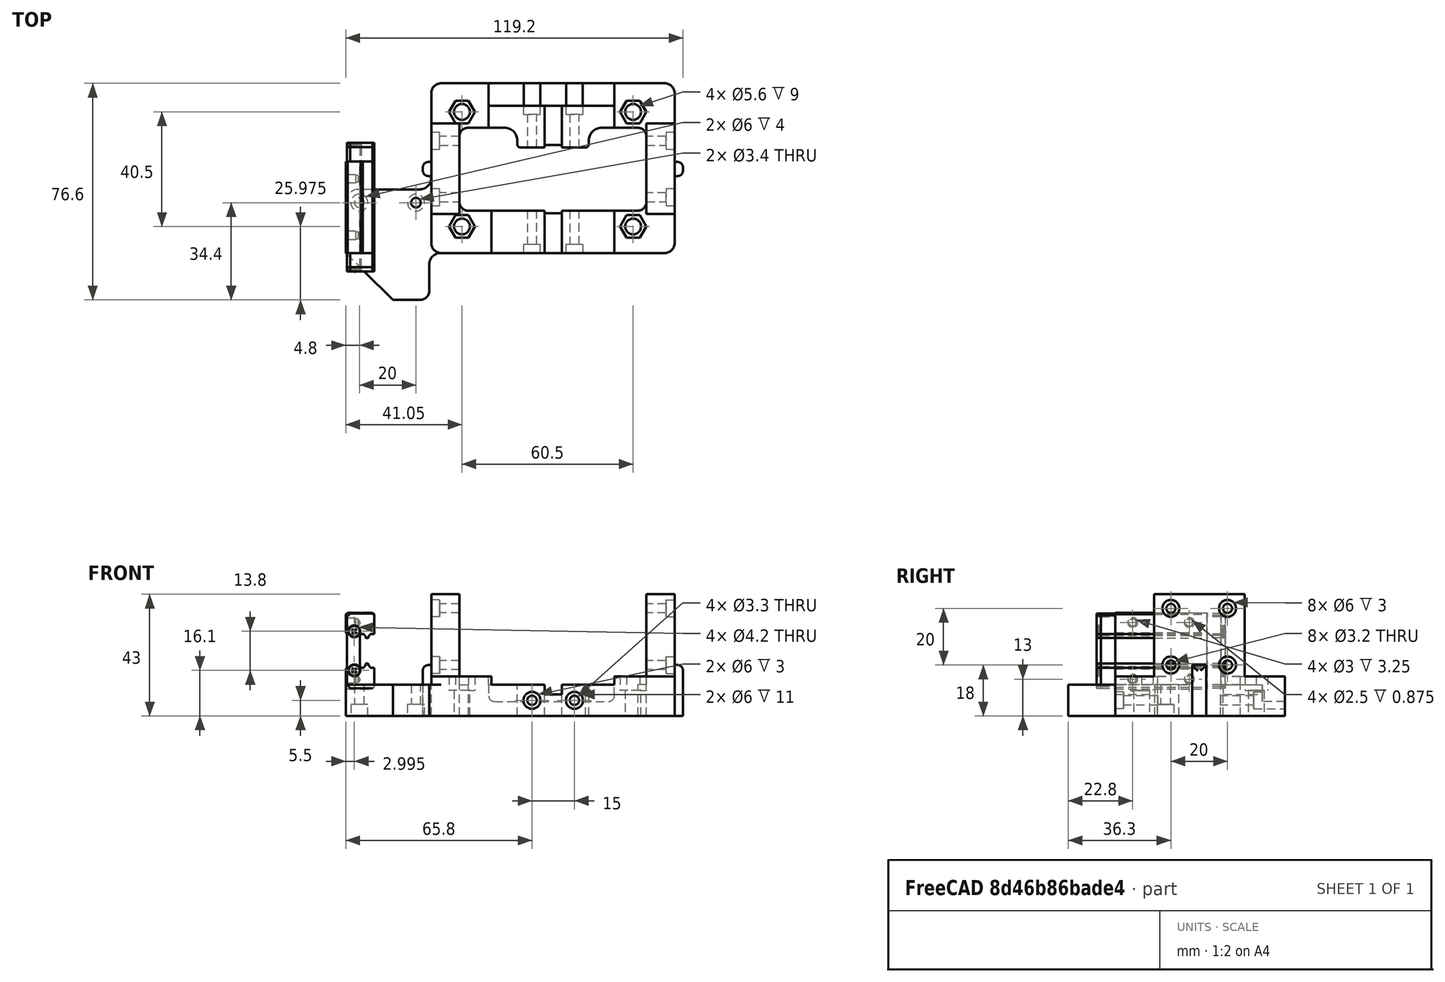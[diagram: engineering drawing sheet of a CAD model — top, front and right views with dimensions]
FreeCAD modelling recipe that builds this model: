
FCSTD DOCUMENT  (FreeCAD 0.19R24291 (Git))
Label: Carriage Mount v2
License: All rights reserved
LicenseURL: http://en.wikipedia.org/wiki/All_rights_reserved
objects: Sketcher::SketchObject×15, PartDesign::Pocket×10, Part::Feature×9, PartDesign::Pad×5, Mesh::Feature×2, PartDesign::Fillet×2, App::Part×1, PartDesign::Body×1, Part::Fillet×1
note: 60 computed .brp shape members not serialized (recipe doc carries the construction recipe); baked Part::Feature solids carry a one-line shape summary decoded from their .brp

FEATURE [Mesh::Feature] y_axis_bed_carriage
  Placement = pos=(-82,-78.3,0) rot=(0,0,1;0rad)
FEATURE [Mesh::Feature] _a__y_belt_clip_x2  label="[a]_y_belt_clip_x2"
  Placement = pos=(-67,-7,115.5) rot=(1,0,0;4.71239rad)
FEATURE [Part::Feature] Part__Feature122  label="MGN12H, LINEAR GUIDE BLOCK v008"
  Placement = pos=(-22.7,16.2,23) rot=(0.57735,-0.57735,0.57735;2.0944rad)
  shape: bbox 4.316 x 1.614 x 4.52 mm, 16 faces (baked)
FEATURE [Part::Feature] Part__Feature121  label="MGN12H, LINEAR GUIDE BLOCK v007"
  Placement = pos=(-22.7,16.2,23) rot=(0.57735,-0.57735,0.57735;2.0944rad)
  shape: bbox 4.36 x 1.614 x 4.223 mm, 16 faces (baked)
FEATURE [Part::Feature] Part__Feature115  label="MGN12H, LINEAR GUIDE BLOCK v1"
  Placement = pos=(-22.7,16.2,23) rot=(0.57735,-0.57735,0.57735;2.0944rad)
  shape: bbox 10 x 32.4 x 27 mm, 66 faces (baked)
FEATURE [Part::Feature] Part__Feature123  label="MGN12H, LINEAR GUIDE BLOCK v009"
  Placement = pos=(-22.7,16.2,23) rot=(0.57735,-0.57735,0.57735;2.0944rad)
  shape: bbox 4.36 x 1.614 x 4.223 mm, 16 faces (baked)
FEATURE [Part::Feature] Part__Feature119  label="MGN12H, LINEAR GUIDE BLOCK v005"
  Placement = pos=(-22.7,16.2,23) rot=(0.57735,-0.57735,0.57735;2.0944rad)
  shape: bbox 9.6 x 1.5 x 26.4 mm, 42 faces (baked)
FEATURE [Part::Feature] Part__Feature120  label="MGN12H, LINEAR GUIDE BLOCK v006"
  Placement = pos=(-22.7,16.2,23) rot=(0.57735,-0.57735,0.57735;2.0944rad)
  shape: bbox 4.316 x 1.614 x 4.52 mm, 16 faces (baked)
FEATURE [Part::Feature] Part__Feature118  label="MGN12H, LINEAR GUIDE BLOCK v004"
  Placement = pos=(-22.7,16.2,23) rot=(0.57735,-0.57735,0.57735;2.0944rad)
  shape: bbox 9.6 x 1.5 x 26.4 mm, 42 faces (baked)
FEATURE [Part::Feature] Part__Feature116  label="MGN12H, LINEAR GUIDE BLOCK v002"
  Placement = pos=(-22.7,16.2,23) rot=(0.57735,-0.57735,0.57735;2.0944rad)
  shape: bbox 9.6 x 5 x 26.4 mm, 40 faces (baked)
FEATURE [Part::Feature] Part__Feature117  label="MGN12H, LINEAR GUIDE BLOCK v003"
  Placement = pos=(-22.7,16.2,23) rot=(0.57735,-0.57735,0.57735;2.0944rad)
  shape: bbox 9.6 x 5 x 26.4 mm, 40 faces (baked)
FEATURE [App::Part] MGN12H__LINEAR_GUIDE_BLOCK_v1  label="MGN12H, LINEAR GUIDE BLOCK v010"
  Group = -> [Part__Feature115,Part__Feature116,Part__Feature117,Part__Feature118,Part__Feature119,Part__Feature120,Part__Feature121,Part__Feature122,Part__Feature123]
  Origin = -> Origin028
  Placement = pos=(40.5,13.5,5) rot=(0,0,1;0rad)
FEATURE [Sketcher::SketchObject] Sketch
  FullyConstrained = true
  MapMode = 5
  Support = -> [XY_Plane]
  sketch-geometry (49):
    g0: LineSegment StartX=3.3 StartY=0 StartZ=0 EndX=82.5 EndY=0 EndZ=0
    g1: LineSegment StartX=86 StartY=3.5 StartZ=0 EndX=86 EndY=56.5 EndZ=0
    g2: LineSegment StartX=82.5 StartY=60 StartZ=0 EndX=3.5 EndY=60 EndZ=0
    g3: LineSegment StartX=0 StartY=56.5 StartZ=0 EndX=0 EndY=26.5 EndZ=0
    g4: ArcOfCircle CenterX=82.5 CenterY=3.5 CenterZ=0 NormalX=0 NormalY=0 NormalZ=1 AngleXU=0 Radius=3.5 StartAngle=4.71239 EndAngle=6.28319
    g5: ArcOfCircle CenterX=82.5 CenterY=56.5 CenterZ=0 NormalX=0 NormalY=0 NormalZ=1 AngleXU=0 Radius=3.5 StartAngle=7e-16 EndAngle=1.5708
    g6: ArcOfCircle CenterX=3.5 CenterY=56.5 CenterZ=0 NormalX=0 NormalY=0 NormalZ=1 AngleXU=0 Radius=3.5 StartAngle=1.5708 EndAngle=3.14159
    g7: ArcOfCircle CenterX=3.3 CenterY=-4 CenterZ=0 NormalX=0 NormalY=0 NormalZ=1 AngleXU=0 Radius=4 StartAngle=1.5708 EndAngle=3.14159
    g8: LineSegment StartX=-4 StartY=22.5 StartZ=0 EndX=-25.6 EndY=22.5 EndZ=0
    g9: LineSegment StartX=-30.2 StartY=17.9 StartZ=0 EndX=-30.2 EndY=0 EndZ=0
    g10: LineSegment StartX=-30.2 StartY=0 StartZ=0 EndX=-13.6 EndY=-16.6 EndZ=0
    g11: LineSegment StartX=-13.6 StartY=-16.6 StartZ=0 EndX=-4 EndY=-16.6 EndZ=0
    g12: LineSegment StartX=-0.7 StartY=-13.3 StartZ=0 EndX=-0.7 EndY=-4 EndZ=0
    g13: ArcOfCircle CenterX=-4 CenterY=-13.3 CenterZ=0 NormalX=0 NormalY=0 NormalZ=1 AngleXU=0 Radius=3.3 StartAngle=4.71239 EndAngle=6.28319
    g14: ArcOfCircle CenterX=-4 CenterY=26.5 CenterZ=0 NormalX=0 NormalY=0 NormalZ=1 AngleXU=0 Radius=4 StartAngle=4.71239 EndAngle=6.28319
    g15: ArcOfCircle CenterX=-25.6 CenterY=17.9 CenterZ=0 NormalX=0 NormalY=0 NormalZ=1 AngleXU=0 Radius=4.6 StartAngle=1.5708 EndAngle=3.14159
    g16: Circle CenterX=-25.4 CenterY=17.8 CenterZ=0 NormalX=0 NormalY=0 NormalZ=1 AngleXU=0 Radius=1.7
    g17: Circle CenterX=-5.4 CenterY=17.8 CenterZ=0 NormalX=0 NormalY=0 NormalZ=1 AngleXU=0 Radius=1.7
    g18: Circle CenterX=10.85 CenterY=9.375 CenterZ=0 NormalX=0 NormalY=0 NormalZ=1 AngleXU=0 Radius=2.8
    g19: Circle CenterX=10.85 CenterY=49.875 CenterZ=0 NormalX=0 NormalY=0 NormalZ=1 AngleXU=0 Radius=2.8
    g20: LineSegment StartX=10.85 StartY=9.375 StartZ=0 EndX=10.85 EndY=49.875 EndZ=0
    g21: Circle CenterX=71.35 CenterY=9.375 CenterZ=0 NormalX=0 NormalY=0 NormalZ=1 AngleXU=0 Radius=2.8
    g22: LineSegment StartX=10.85 StartY=9.375 StartZ=0 EndX=71.35 EndY=9.375 EndZ=0
    g23: Circle CenterX=71.35 CenterY=49.875 CenterZ=0 NormalX=0 NormalY=0 NormalZ=1 AngleXU=0 Radius=2.8
    g24: LineSegment StartX=71.35 StartY=9.375 StartZ=0 EndX=71.35 EndY=49.875 EndZ=0
    g25: LineSegment StartX=13 StartY=44.275 StartZ=0 EndX=25.9042 EndY=44.275 EndZ=0
    g26: LineSegment StartX=76 StartY=41.2768 StartZ=0 EndX=76 EndY=17.975 EndZ=0
    g27: LineSegment StartX=73 StartY=14.975 StartZ=0 EndX=46.2 EndY=14.975 EndZ=0
    g28: LineSegment StartX=10 StartY=17.9683 StartZ=0 EndX=10 EndY=41.275 EndZ=0
    g29: ArcOfCircle CenterX=13 CenterY=17.9683 CenterZ=0 NormalX=0 NormalY=0 NormalZ=1 AngleXU=0 Radius=3 StartAngle=3.14159 EndAngle=4.77911
    g30: ArcOfCircle CenterX=73 CenterY=17.975 CenterZ=0 NormalX=0 NormalY=0 NormalZ=1 AngleXU=0 Radius=3 StartAngle=4.71239 EndAngle=6.28319
    g31: ArcOfCircle CenterX=13 CenterY=41.275 CenterZ=0 NormalX=0 NormalY=0 NormalZ=1 AngleXU=0 Radius=3 StartAngle=1.5708 EndAngle=3.14159
    g32: ArcOfCircle CenterX=73 CenterY=41.2768 CenterZ=0 NormalX=0 NormalY=0 NormalZ=1 AngleXU=0 Radius=3 StartAngle=1e-15 EndAngle=1.53606
    g33: LineSegment StartX=30.4 StartY=39.7792 StartZ=0 EndX=30.4 EndY=38.475 EndZ=0
    g34: LineSegment StartX=31.6 StartY=37.275 StartZ=0 EndX=40 EndY=37.275 EndZ=0
    g35: LineSegment StartX=55.7 StartY=38.4708 StartZ=0 EndX=55.7 EndY=39.775 EndZ=0
    g36: LineSegment StartX=60.2 StartY=44.275 StartZ=0 EndX=73.1042 EndY=44.275 EndZ=0
    g37: ArcOfCircle CenterX=25.9042 CenterY=39.7792 CenterZ=0 NormalX=0 NormalY=0 NormalZ=1 AngleXU=0 Radius=4.49583 StartAngle=1e-16 EndAngle=1.5708
    g38: ArcOfCircle CenterX=60.2 CenterY=39.775 CenterZ=0 NormalX=0 NormalY=0 NormalZ=1 AngleXU=0 Radius=4.5 StartAngle=1.5708 EndAngle=3.14159
    g39: ArcOfCircle CenterX=54.5 CenterY=38.4708 CenterZ=0 NormalX=0 NormalY=0 NormalZ=1 AngleXU=0 Radius=1.2 StartAngle=4.79582 EndAngle=6.28319
    g40: ArcOfCircle CenterX=31.6 CenterY=38.475 CenterZ=0 NormalX=0 NormalY=0 NormalZ=1 AngleXU=0 Radius=1.2 StartAngle=3.14159 EndAngle=4.71239
    g41: LineSegment StartX=40 StartY=37.275 StartZ=0 EndX=40 EndY=38.175 EndZ=0
    g42: LineSegment StartX=40 StartY=38.175 StartZ=0 EndX=46.2 EndY=38.175 EndZ=0
    g43: LineSegment StartX=46.2 StartY=38.175 StartZ=0 EndX=46.2 EndY=37.275 EndZ=0
    g44: LineSegment StartX=46.2 StartY=37.275 StartZ=0 EndX=54.6 EndY=37.275 EndZ=0
    g45: LineSegment StartX=40 StartY=14.975 StartZ=0 EndX=40 EndY=14.075 EndZ=0
    g46: LineSegment StartX=40 StartY=14.075 StartZ=0 EndX=46.2 EndY=14.075 EndZ=0
    g47: LineSegment StartX=46.2 StartY=14.075 StartZ=0 EndX=46.2 EndY=14.975 EndZ=0
    g48: LineSegment StartX=40 StartY=14.975 StartZ=0 EndX=13.2 EndY=14.975 EndZ=0
  constraints (131):
    c: Horizontal(g0)
    c: Horizontal(g2)
    c: Vertical(g1)
    c: Vertical(g3)
    c: Tangent(g0,g4) = -1.5708
    c: Tangent(g1,g4) = -1.5708
    c: Tangent(g1,g5) = -1.5708
    c: Tangent(g2,g5) = -1.5708
    c: Tangent(g3,g6) = -1.5708
    c: Tangent(g2,g6) = -1.5708
    c: PointOnObject(g0,g-1)
    c: DistanceY(g-1,g2) = 60
    c: Radius(g6) = 3.5
    c: Coincident(g7,g0)
    c: Horizontal(g8)
    c: PointOnObject(g9,g-1)
    c: Vertical(g9)
    c: Coincident(g9,g10)
    c: Coincident(g10,g11)
    c: Horizontal(g11)
    c: Coincident(g12,g7)
    c: Vertical(g12)
    c: Tangent(g11,g13) = -1.5708
    c: Tangent(g12,g13) = -1.5708
    c: Tangent(g8,g14) = 1.5708
    c: Tangent(g3,g14) = 1.5708
    c: Tangent(g9,g15) = -1.5708
    c: Tangent(g8,g15) = -1.5708
    c: PointOnObject(g3,g-2)
    c: Equal(g6,g5)
    c: Equal(g5,g4)
    c: Angle(g7) = 1.5708
    c: DistanceY(g-1,g8) = 22.5
    c: DistanceX(g9,g-1) = 30.2
    c: DistanceY(g11,g-1) = 16.6
    c: DistanceX(g7,g-1) = 0.7
    c: Distance(g12) = 9.3
    c: Radius(g7) = 4
    c: DistanceX(g11,g11) = 9.6
    c: Radius(g15) = 4.6
    c: Radius(g14) = 4
    c: DistanceX(g3,g1) = 86
    c: DistanceY(g7,g-1) = 4
    c: Radius(g16) = 1.7
    c: Equal(g16,g17) = 1.7
    c: Horizontal(g16,g17)
    c: DistanceX(g17,g-1) = 5.4
    c: DistanceX(g16,g17) = 20
    c: DistanceY(g-1,g17) = 17.8
    c: Radius(g18) = 2.8
    c: DistanceX(g-1,g18) = 10.85
    c: DistanceY(g-1,g18) = 9.375
    c: Radius(g19) = 2.8
    c: Coincident(g18,g20)
    c: Coincident(g19,g20)
    c: Distance(g20) = 40.5
    c: Angle(g20) = 1.5708
    c: Radius(g21) = 2.8
    c: Coincident(g18,g22)
    c: Coincident(g21,g22)
    c: Distance(g22) = 60.5
    c: Perpendicular(g22,g20)
    c: Radius(g23) = 2.8
    c: Coincident(g21,g24)
    c: Coincident(g23,g24)
    c: Equal(g20,g24)
    c: Parallel(g24,g20)
    c: Horizontal(g25)
    c: Horizontal(g27)
    c: Vertical(g26)
    c: Vertical(g28)
    c: Tangent(g28,g29) = 1.5708
    c: Coincident(g48,g29) = 1.5708
    c: Tangent(g27,g30) = 1.5708
    c: Tangent(g26,g30) = 1.5708
    c: Tangent(g28,g31) = 1.5708
    c: Tangent(g25,g31) = 1.5708
    c: Coincident(g36,g32) = 1.5708
    c: Tangent(g26,g32) = 1.5708
    c: Equal(g29,g31)
    c: Equal(g31,g32)
    c: Equal(g32,g30)
    c: Radius(g29) = 3
    c: DistanceX(g-1,g28) = 10
    c: DistanceX(g26,g1) = 10
    c: DistanceY(g18,g48) = 5.6
    c: DistanceY(g25,g19) = 5.6
    c: Vertical(g33)
    c: Horizontal(g34)
    c: Vertical(g35)
    c: Tangent(g25,g36)
    c: Tangent(g25,g37) = 1.5708
    c: Tangent(g33,g37) = 1.5708
    c: Tangent(g35,g38) = 1.5708
    c: Tangent(g36,g38) = 1.5708
    c: Coincident(g44,g39) = -1.5708
    c: Tangent(g35,g39) = -1.5708
    c: Tangent(g33,g40) = -1.5708
    c: Tangent(g34,g40) = -1.5708
    c: Equal(g40,g39)
    c: DistanceY(g34,g25) = 7
    c: DistanceX(g28,g33) = 20.4
    c: DistanceX(g33,g35) = 25.3
    c: Radius(g40) = 1.2
    c: Equal(g33,g35)
    c: Equal(g25,g36)
    c: Radius(g38) = 4.5
    c: Vertical(g41)
    c: Coincident(g41,g42)
    c: Horizontal(g42)
    c: Coincident(g42,g43)
    c: Vertical(g43)
    c: Coincident(g34,g41)
    c: Coincident(g44,g43)
    c: Tangent(g34,g44)
    c: Equal(g34,g44)
    c: DistanceX(g42,g42) = 6.2
    c: DistanceX(g34,g34) = 8.4
    c: DistanceY(g43,g43) = 0.9
    c: Coincident(g45,g46)
    c: Horizontal(g46)
    c: Coincident(g46,g47)
    c: Vertical(g47)
    c: Vertical(g45)
    c: Equal(g42,g46)
    c: Equal(g43,g47)
    c: Coincident(g27,g47)
    c: Coincident(g48,g45)
    c: Tangent(g27,g48)
    c: Equal(g48,g27)
    c: DistanceX(g48,g48) = 26.8
FEATURE [PartDesign::Pad] Pad
  Direction = (1,1,1)
  Length = 11
  Length2 = 100
  Profile = -> Sketch
  Type = 0
FEATURE [Sketcher::SketchObject] Sketch001
  ExternalGeometry = -> [Pad]
  FullyConstrained = true
  MapMode = 5
  Placement = pos=(0,0,11) rot=(0,0,1;0rad)
  Support = -> [Pad]
  sketch-geometry (24):
    g0: LineSegment StartX=3.5 StartY=0 StartZ=0 EndX=21.3 EndY=0 EndZ=0
    g1: LineSegment StartX=21.3 StartY=0 StartZ=0 EndX=21.3 EndY=14.975 EndZ=0
    g2: LineSegment StartX=21.3 StartY=14.975 StartZ=0 EndX=12.9933 EndY=14.975 EndZ=0
    g3: LineSegment StartX=10 StartY=17.9683 StartZ=0 EndX=10 EndY=41.275 EndZ=0
    g4: LineSegment StartX=20.3 StartY=44.275 StartZ=0 EndX=20.3 EndY=60 EndZ=0
    g5: LineSegment StartX=20.3 StartY=60 StartZ=0 EndX=3.5 EndY=60 EndZ=0
    g6: LineSegment StartX=0 StartY=56.5 StartZ=0 EndX=0 EndY=3.5 EndZ=0
    g7: ArcOfCircle CenterX=12.9933 CenterY=17.9683 CenterZ=0 NormalX=0 NormalY=0 NormalZ=1 AngleXU=0 Radius=2.99333 StartAngle=3.14159 EndAngle=4.71239
    g8: ArcOfCircle CenterX=13 CenterY=41.275 CenterZ=0 NormalX=0 NormalY=0 NormalZ=1 AngleXU=0 Radius=3 StartAngle=1.5708 EndAngle=3.14159
    g9: ArcOfCircle CenterX=3.5 CenterY=56.5 CenterZ=0 NormalX=0 NormalY=0 NormalZ=1 AngleXU=0 Radius=3.5 StartAngle=1.5708 EndAngle=3.14159
    g10: LineSegment StartX=13 StartY=44.275 StartZ=0 EndX=20.3 EndY=44.275 EndZ=0
    g11: ArcOfCircle CenterX=3.5 CenterY=3.5 CenterZ=0 NormalX=0 NormalY=0 NormalZ=1 AngleXU=0 Radius=3.5 StartAngle=3.14159 EndAngle=4.71239
    g12: LineSegment StartX=64.7 StartY=0 StartZ=0 EndX=64.7 EndY=14.975 EndZ=0
    g13: LineSegment StartX=64.7 StartY=14.975 StartZ=0 EndX=73 EndY=14.975 EndZ=0
    g14: LineSegment StartX=76 StartY=17.975 StartZ=0 EndX=76 EndY=41.2768 EndZ=0
    g15: LineSegment StartX=73.0018 StartY=44.275 StartZ=0 EndX=64.7018 EndY=44.275 EndZ=0
    g16: LineSegment StartX=64.7018 StartY=44.275 StartZ=0 EndX=64.7018 EndY=60 EndZ=0
    g17: LineSegment StartX=64.7018 StartY=60 StartZ=0 EndX=82.5 EndY=60 EndZ=0
    g18: LineSegment StartX=86 StartY=56.5 StartZ=0 EndX=86 EndY=3.5 EndZ=0
    g19: LineSegment StartX=82.5 StartY=0 StartZ=0 EndX=64.7 EndY=0 EndZ=0
    g20: ArcOfCircle CenterX=73 CenterY=17.975 CenterZ=0 NormalX=0 NormalY=0 NormalZ=1 AngleXU=0 Radius=3 StartAngle=4.71239 EndAngle=6.28319
    g21: ArcOfCircle CenterX=73.0018 CenterY=41.2768 CenterZ=0 NormalX=0 NormalY=0 NormalZ=1 AngleXU=0 Radius=2.99819 StartAngle=1.1e-15 EndAngle=1.5708
    g22: ArcOfCircle CenterX=82.5 CenterY=56.5 CenterZ=0 NormalX=0 NormalY=0 NormalZ=1 AngleXU=0 Radius=3.5 StartAngle=0 EndAngle=1.5708
    g23: ArcOfCircle CenterX=82.5 CenterY=3.5 CenterZ=0 NormalX=0 NormalY=0 NormalZ=1 AngleXU=0 Radius=3.5 StartAngle=4.71239 EndAngle=6.28319
  constraints (56):
    c: PointOnObject(g0,g-1)
    c: Coincident(g0,g1)
    c: PointOnObject(g1,g-3)
    c: Vertical(g1)
    c: Coincident(g1,g2)
    c: Horizontal(g2)
    c: PointOnObject(g4,g-6)
    c: Vertical(g4)
    c: Coincident(g4,g5)
    c: Tangent(g3,g7) = 1.5708
    c: Tangent(g2,g7) = 1.5708
    c: Coincident(g3,g-4)
    c: DistanceX(g-1,g0) = 21.3
    c: Tangent(g3,g8) = 1.5708
    c: Coincident(g-5,g8) = 1.5708
    c: Tangent(g6,g9) = -1.5708
    c: Tangent(g5,g9) = -1.5708
    c: Coincident(g10,g8)
    c: Coincident(g10,g4)
    c: Horizontal(g10)
    c: DistanceX(g6,g4) = 20.3
    c: Coincident(g5,g-6)
    c: PointOnObject(g6,g-2)
    c: Coincident(g3,g-4)
    c: Tangent(g6,g11) = -1.5708
    c: Tangent(g0,g11) = -1.5708
    c: Radius(g11) = 3.5
    c: PointOnObject(g6,g-2)
    c: PointOnObject(g0,g-1)
    c: PointOnObject(g12,g-1)
    c: Vertical(g12)
    c: Coincident(g12,g13)
    c: Horizontal(g15)
    c: Coincident(g15,g16)
    c: PointOnObject(g16,g-6)
    c: Vertical(g16)
    c: Coincident(g16,g17)
    c: Vertical(g18)
    c: Coincident(g19,g12)
    c: Tangent(g13,g20) = -1.5708
    c: Tangent(g14,g20) = -1.5708
    c: Tangent(g15,g21) = -1.5708
    c: Tangent(g14,g21) = -1.5708
    c: Tangent(g17,g22) = 1.5708
    c: Tangent(g18,g22) = 1.5708
    c: Tangent(g19,g23) = 1.5708
    c: Tangent(g18,g23) = 1.5708
    c: Coincident(g18,g-10)
    c: DistanceX(g12,g18) = 21.3
    c: Horizontal(g19)
    c: Coincident(g13,g-8)
    c: Coincident(g14,g-9)
    c: Coincident(g14,g-9)
    c: PointOnObject(g15,g-7)
    c: Equal(g13,g15)
    c: Coincident(g17,g-6)
FEATURE [PartDesign::Pad] Pad001
  BaseFeature = -> Pad
  Direction = (1,1,1)
  Length = 3
  Length2 = 100
  Profile = -> Sketch001
  Type = 0
FEATURE [Sketcher::SketchObject] Sketch002
  ExternalGeometry = -> [Pad]
  FullyConstrained = true
  MapMode = 5
  Placement = pos=(0,0,14) rot=(0,0,1;0rad)
  Support = -> [Pad001]
  sketch-geometry (28):
    g0: LineSegment StartX=13.1594 StartY=5.375 StartZ=0 EndX=15.4688 EndY=9.375 EndZ=0
    g1: LineSegment StartX=15.4688 StartY=9.375 StartZ=0 EndX=13.1594 EndY=13.375 EndZ=0
    g2: LineSegment StartX=13.1594 StartY=13.375 StartZ=0 EndX=8.5406 EndY=13.375 EndZ=0
    g3: LineSegment StartX=8.5406 StartY=13.375 StartZ=0 EndX=6.2312 EndY=9.375 EndZ=0
    g4: LineSegment StartX=6.2312 StartY=9.375 StartZ=0 EndX=8.5406 EndY=5.375 EndZ=0
    g5: LineSegment StartX=8.5406 StartY=5.375 StartZ=0 EndX=13.1594 EndY=5.375 EndZ=0
    g6: Circle CenterX=10.85 CenterY=9.375 CenterZ=0 NormalX=0 NormalY=0 NormalZ=1 AngleXU=0 Radius=4.6188
    g7: LineSegment StartX=13.1594 StartY=45.875 StartZ=0 EndX=15.4688 EndY=49.875 EndZ=0
    g8: LineSegment StartX=15.4688 StartY=49.875 StartZ=0 EndX=13.1594 EndY=53.875 EndZ=0
    g9: LineSegment StartX=13.1594 StartY=53.875 StartZ=0 EndX=8.5406 EndY=53.875 EndZ=0
    g10: LineSegment StartX=8.5406 StartY=53.875 StartZ=0 EndX=6.2312 EndY=49.875 EndZ=0
    g11: LineSegment StartX=6.2312 StartY=49.875 StartZ=0 EndX=8.5406 EndY=45.875 EndZ=0
    g12: LineSegment StartX=8.5406 StartY=45.875 StartZ=0 EndX=13.1594 EndY=45.875 EndZ=0
    g13: Circle CenterX=10.85 CenterY=49.875 CenterZ=0 NormalX=0 NormalY=0 NormalZ=1 AngleXU=0 Radius=4.6188
    g14: LineSegment StartX=73.6594 StartY=45.875 StartZ=0 EndX=75.9688 EndY=49.875 EndZ=0
    g15: LineSegment StartX=75.9688 StartY=49.875 StartZ=0 EndX=73.6594 EndY=53.875 EndZ=0
    g16: LineSegment StartX=73.6594 StartY=53.875 StartZ=0 EndX=69.0406 EndY=53.875 EndZ=0
    g17: LineSegment StartX=69.0406 StartY=53.875 StartZ=0 EndX=66.7312 EndY=49.875 EndZ=0
    g18: LineSegment StartX=66.7312 StartY=49.875 StartZ=0 EndX=69.0406 EndY=45.875 EndZ=0
    g19: LineSegment StartX=69.0406 StartY=45.875 StartZ=0 EndX=73.6594 EndY=45.875 EndZ=0
    g20: Circle CenterX=71.35 CenterY=49.875 CenterZ=0 NormalX=0 NormalY=0 NormalZ=1 AngleXU=0 Radius=4.6188
    g21: LineSegment StartX=73.6594 StartY=5.375 StartZ=0 EndX=75.9688 EndY=9.375 EndZ=0
    g22: LineSegment StartX=75.9688 StartY=9.375 StartZ=0 EndX=73.6594 EndY=13.375 EndZ=0
    g23: LineSegment StartX=73.6594 StartY=13.375 StartZ=0 EndX=69.0406 EndY=13.375 EndZ=0
    g24: LineSegment StartX=69.0406 StartY=13.375 StartZ=0 EndX=66.7312 EndY=9.375 EndZ=0
    g25: LineSegment StartX=66.7312 StartY=9.375 StartZ=0 EndX=69.0406 EndY=5.375 EndZ=0
    g26: LineSegment StartX=69.0406 StartY=5.375 StartZ=0 EndX=73.6594 EndY=5.375 EndZ=0
    g27: Circle CenterX=71.35 CenterY=9.375 CenterZ=0 NormalX=0 NormalY=0 NormalZ=1 AngleXU=0 Radius=4.6188
  constraints (64):
    c: Coincident(g0,g1)
    c: Coincident(g1,g2)
    c: Coincident(g2,g3)
    c: Coincident(g3,g4)
    c: Coincident(g4,g5)
    c: Coincident(g5,g0)
    c: Equal(g0, g1-g5) x5
    c: PointOnObject(g0,g6)
    c: PointOnObject(g1,g6)
    c: PointOnObject(g2,g6)
    c: PointOnObject(g3,g6)
    c: PointOnObject(g4,g6)
    c: PointOnObject(g5,g6)
    c: Coincident(g6,g-3)
    c: Horizontal(g2)
    c: DistanceY(g4,g2) = 8
    c: Coincident(g7,g8)
    c: Coincident(g8,g9)
    c: Coincident(g9,g10)
    c: Coincident(g10,g11)
    c: Coincident(g11,g12)
    c: Coincident(g12,g7)
    c: Equal(g7, g8-g12) x5
    c: PointOnObject(g7,g13)
    c: PointOnObject(g8,g13)
    c: PointOnObject(g9,g13)
    c: PointOnObject(g10,g13)
    c: PointOnObject(g11,g13)
    c: PointOnObject(g12,g13)
    c: Coincident(g13,g-4)
    c: Coincident(g14,g15)
    c: Coincident(g15,g16)
    c: Coincident(g16,g17)
    c: Coincident(g17,g18)
    c: Coincident(g18,g19)
    c: Coincident(g19,g14)
    c: Equal(g14, g15-g19) x5
    c: PointOnObject(g14,g20)
    c: PointOnObject(g15,g20)
    c: PointOnObject(g16,g20)
    c: PointOnObject(g17,g20)
    c: PointOnObject(g18,g20)
    c: PointOnObject(g19,g20)
    c: Coincident(g20,g-5)
    c: Coincident(g21,g22)
    c: Coincident(g22,g23)
    c: Coincident(g23,g24)
    c: Coincident(g24,g25)
    c: Coincident(g25,g26)
    c: Coincident(g26,g21)
    c: Equal(g21, g22-g26) x5
    c: PointOnObject(g21,g27)
    c: PointOnObject(g22,g27)
    c: PointOnObject(g23,g27)
    c: PointOnObject(g24,g27)
    c: PointOnObject(g25,g27)
    c: PointOnObject(g26,g27)
    c: Coincident(g27,g-6)
    c: Horizontal(g23)
    c: DistanceY(g25,g23) = 8
    c: Horizontal(g9)
    c: Horizontal(g16)
    c: DistanceY(g11,g9) = 8
    c: DistanceY(g18,g16) = 8
FEATURE [PartDesign::Pocket] Pocket
  BaseFeature = -> Pad001
  Length = 5
  Length2 = 100
  Profile = -> Sketch002
  Type = 0
FEATURE [Sketcher::SketchObject] Sketch003
  ExternalGeometry = -> [Pocket]
  FullyConstrained = true
  MapMode = 5
  Placement = pos=(0,0,0) rot=(1,0,0;1.5708rad)
  Support = -> [Pocket]
  sketch-geometry (2):
    g0: Circle CenterX=35.6 CenterY=5.5 CenterZ=0 NormalX=0 NormalY=0 NormalZ=1 AngleXU=0 Radius=1.65
    g1: Circle CenterX=50.6 CenterY=5.5 CenterZ=0 NormalX=0 NormalY=0 NormalZ=1 AngleXU=0 Radius=1.65
  constraints (6):
    c: Radius(g0) = 1.65
    c: Equal(g0,g1)
    c: DistanceX(g0,g1) = 15
    c: DistanceX(g-1,g0) = 35.6
    c: DistanceY(g-1,g0) = 5.5
    c: Horizontal(g0,g1)
FEATURE [PartDesign::Pocket] Pocket001
  BaseFeature = -> Pocket
  Length = 60
  Length2 = 100
  Profile = -> Sketch003
  Type = 0
FEATURE [Sketcher::SketchObject] Sketch004
  ExternalGeometry = -> [Pocket001]
  FullyConstrained = true
  MapMode = 5
  Placement = pos=(0,0,0) rot=(1,0,0;1.5708rad)
  Support = -> [Pocket001]
  sketch-geometry (2):
    g0: Circle CenterX=35.6 CenterY=5.5 CenterZ=0 NormalX=0 NormalY=0 NormalZ=1 AngleXU=0 Radius=3
    g1: Circle CenterX=50.6 CenterY=5.5 CenterZ=0 NormalX=0 NormalY=0 NormalZ=1 AngleXU=0 Radius=3
  constraints (4):
    c: Radius(g0) = 3
    c: Equal(g0,g1)
    c: Coincident(g1,g-4)
    c: Coincident(g0,g-3)
FEATURE [PartDesign::Pocket] Pocket002
  BaseFeature = -> Pocket001
  Length = 3
  Length2 = 100
  Profile = -> Sketch004
  Type = 0
FEATURE [Sketcher::SketchObject] Sketch005
  ExternalGeometry = -> [Pocket002]
  FullyConstrained = true
  MapMode = 5
  Placement = pos=(0,0,0) rot=(1,0,0;3.14159rad)
  Support = -> [Pocket002]
  sketch-geometry (2):
    g0: Circle CenterX=-25.4 CenterY=-17.8 CenterZ=0 NormalX=0 NormalY=0 NormalZ=1 AngleXU=0 Radius=3
    g1: Circle CenterX=-5.4 CenterY=-17.8 CenterZ=0 NormalX=0 NormalY=0 NormalZ=1 AngleXU=0 Radius=3
  constraints (4):
    c: Coincident(g0,g-3)
    c: Coincident(g1,g-4)
    c: Equal(g0,g1)
    c: Radius(g0) = 3
FEATURE [PartDesign::Pocket] Pocket003  label="Belt Cutout"
  BaseFeature = -> Pocket002
  Length = 4
  Length2 = 100
  Profile = -> Sketch005
  Type = 0
FEATURE [Sketcher::SketchObject] Sketch006
  ExternalGeometry = -> [Pocket003]
  FullyConstrained = true
  MapMode = 5
  Placement = pos=(0,0,14) rot=(0,0,1;0rad)
  Support = -> [Pocket003]
  sketch-geometry (8):
    g0: LineSegment StartX=0 StartY=13.8 StartZ=0 EndX=10 EndY=13.8 EndZ=0
    g1: LineSegment StartX=10 StartY=13.8 StartZ=0 EndX=10 EndY=45.8 EndZ=0
    g2: LineSegment StartX=10 StartY=45.8 StartZ=0 EndX=0 EndY=45.8 EndZ=0
    g3: LineSegment StartX=0 StartY=45.8 StartZ=0 EndX=0 EndY=13.8 EndZ=0
    g4: LineSegment StartX=86 StartY=13.8 StartZ=0 EndX=76 EndY=13.8 EndZ=0
    g5: LineSegment StartX=76 StartY=13.8 StartZ=0 EndX=76 EndY=45.8 EndZ=0
    g6: LineSegment StartX=76 StartY=45.8 StartZ=0 EndX=86 EndY=45.8 EndZ=0
    g7: LineSegment StartX=86 StartY=45.8 StartZ=0 EndX=86 EndY=13.8 EndZ=0
  constraints (24):
    c: Coincident(g0,g1)
    c: Coincident(g1,g2)
    c: Coincident(g2,g3)
    c: Coincident(g3,g0)
    c: Horizontal(g0)
    c: Horizontal(g2)
    c: Vertical(g1)
    c: Vertical(g3)
    c: PointOnObject(g0,g-2)
    c: DistanceX(g2,g2) = 10
    c: DistanceY(g3,g3) = 32
    c: DistanceY(g-1,g0) = 13.8
    c: Coincident(g4,g5)
    c: Coincident(g5,g6)
    c: Coincident(g6,g7)
    c: Coincident(g7,g4)
    c: Horizontal(g4)
    c: Horizontal(g6)
    c: Vertical(g5)
    c: Vertical(g7)
    c: PointOnObject(g4,g-3)
    c: PointOnObject(g-4,g5)
    c: Equal(g3,g7)
    c: DistanceY(g-1,g4) = 13.8
FEATURE [PartDesign::Pad] Pad002  label="MGN12H Supports"
  BaseFeature = -> Pocket003
  Direction = (1,1,1)
  Length = 29
  Length2 = 100
  Profile = -> Sketch006
  Type = 0
FEATURE [Sketcher::SketchObject] Sketch007
  FullyConstrained = true
  MapMode = 5
  Placement = pos=(0,0,0) rot=(0.57735,-0.57735,-0.57735;2.0944rad)
  Support = -> [Pad002]
  sketch-geometry (7):
    g0: Circle CenterX=-39.7 CenterY=18 CenterZ=0 NormalX=0 NormalY=0 NormalZ=1 AngleXU=0 Radius=1.6
    g1: Circle CenterX=-39.7 CenterY=38 CenterZ=0 NormalX=0 NormalY=0 NormalZ=1 AngleXU=0 Radius=1.6
    g2: LineSegment StartX=-39.7 StartY=18 StartZ=0 EndX=-39.7 EndY=38 EndZ=0
    g3: Circle CenterX=-19.7 CenterY=18 CenterZ=0 NormalX=0 NormalY=0 NormalZ=1 AngleXU=0 Radius=1.6
    g4: LineSegment StartX=-39.7 StartY=18 StartZ=0 EndX=-19.7 EndY=18 EndZ=0
    g5: Circle CenterX=-19.7 CenterY=38 CenterZ=0 NormalX=0 NormalY=0 NormalZ=1 AngleXU=0 Radius=1.6
    g6: LineSegment StartX=-19.7 StartY=18 StartZ=0 EndX=-19.7 EndY=38 EndZ=0
  constraints (18):
    c: Radius(g0) = 1.6
    c: DistanceY(g-1,g0) = 18
    c: DistanceX(g0,g-1) = 39.7
    c: Radius(g1) = 1.6
    c: Coincident(g0,g2)
    c: Coincident(g1,g2)
    c: Distance(g2) = 20
    c: Angle(g2) = 1.5708
    c: Radius(g3) = 1.6
    c: Coincident(g0,g4)
    c: Coincident(g3,g4)
    c: Distance(g4) = 20
    c: Perpendicular(g4,g2)
    c: Radius(g5) = 1.6
    c: Coincident(g3,g6)
    c: Coincident(g5,g6)
    c: Equal(g2,g6)
    c: Parallel(g6,g2)
FEATURE [PartDesign::Pocket] Pocket004
  BaseFeature = -> Pad002
  Length = 90
  Length2 = 100
  Profile = -> Sketch007
  Type = 0
FEATURE [Sketcher::SketchObject] Sketch008
  ExternalGeometry = -> [Pocket004]
  FullyConstrained = true
  MapMode = 5
  Placement = pos=(0,0,0) rot=(0.57735,-0.57735,-0.57735;2.0944rad)
  Support = -> [Pocket004]
  sketch-geometry (4):
    g0: Circle CenterX=-39.7 CenterY=38 CenterZ=0 NormalX=0 NormalY=0 NormalZ=1 AngleXU=0 Radius=3
    g1: Circle CenterX=-39.7 CenterY=18 CenterZ=0 NormalX=0 NormalY=0 NormalZ=1 AngleXU=0 Radius=3
    g2: Circle CenterX=-19.7 CenterY=38 CenterZ=0 NormalX=0 NormalY=0 NormalZ=1 AngleXU=0 Radius=3
    g3: Circle CenterX=-19.7 CenterY=18 CenterZ=0 NormalX=0 NormalY=0 NormalZ=1 AngleXU=0 Radius=3
  constraints (8):
    c: Coincident(g0,g-3)
    c: Radius(g0) = 3
    c: Equal(g0,g1) = 3
    c: Coincident(g1,g-6)
    c: Equal(g0,g2) = 3
    c: Coincident(g2,g-4)
    c: Equal(g0,g3) = 3
    c: Coincident(g3,g-5)
FEATURE [PartDesign::Pocket] Pocket005
  BaseFeature = -> Pocket004
  Length = 3
  Length2 = 100
  Profile = -> Sketch008
  Type = 0
FEATURE [Sketcher::SketchObject] Sketch009
  ExternalGeometry = -> [Pocket005]
  FullyConstrained = true
  MapMode = 5
  Placement = pos=(86,0,0) rot=(0.57735,0.57735,0.57735;2.0944rad)
  Support = -> [Pocket005]
  sketch-geometry (4):
    g0: Circle CenterX=19.7 CenterY=38 CenterZ=0 NormalX=0 NormalY=0 NormalZ=1 AngleXU=0 Radius=3
    g1: Circle CenterX=19.7 CenterY=18 CenterZ=0 NormalX=0 NormalY=0 NormalZ=1 AngleXU=0 Radius=3
    g2: Circle CenterX=39.7 CenterY=38 CenterZ=0 NormalX=0 NormalY=0 NormalZ=1 AngleXU=0 Radius=3
    g3: Circle CenterX=39.7 CenterY=18 CenterZ=0 NormalX=0 NormalY=0 NormalZ=1 AngleXU=0 Radius=3
  constraints (8):
    c: Radius(g0) = 3
    c: Equal(g0,g1) = 3
    c: Equal(g0,g2) = 3
    c: Equal(g0,g3) = 3
    c: Coincident(g1,g-6)
    c: Coincident(g3,g-5)
    c: Coincident(g2,g-4)
    c: Coincident(g0,g-3)
FEATURE [PartDesign::Pocket] Pocket006
  BaseFeature = -> Pocket005
  Length = 3
  Length2 = 100
  Profile = -> Sketch009
  Type = 0
FEATURE [Sketcher::SketchObject] Sketch010
  ExternalGeometry = -> [Pocket006]
  FullyConstrained = true
  MapMode = 5
  Placement = pos=(0,0,0) rot=(1,0,0;1.5708rad)
  Support = -> [Pocket006]
  sketch-geometry (4):
    g0: LineSegment StartX=40.05 StartY=11 StartZ=0 EndX=46.15 EndY=11 EndZ=0
    g1: LineSegment StartX=46.15 StartY=11 StartZ=0 EndX=46.15 EndY=7.6 EndZ=0
    g2: LineSegment StartX=46.15 StartY=7.6 StartZ=0 EndX=40.05 EndY=7.6 EndZ=0
    g3: LineSegment StartX=40.05 StartY=7.6 StartZ=0 EndX=40.05 EndY=11 EndZ=0
  constraints (12):
    c: Coincident(g0,g1)
    c: Coincident(g1,g2)
    c: Coincident(g2,g3)
    c: Coincident(g3,g0)
    c: Horizontal(g0)
    c: Horizontal(g2)
    c: Vertical(g1)
    c: Vertical(g3)
    c: PointOnObject(g0,g-4)
    c: DistanceX(g0,g0) = 6.1
    c: DistanceX(g-3,g0) = 4.45
    c: DistanceY(g3,g3) = 3.4
FEATURE [PartDesign::Pocket] Pocket007
  BaseFeature = -> Pocket006
  Length = 60
  Length2 = 100
  Profile = -> Sketch010
  Type = 0
FEATURE [Sketcher::SketchObject] Sketch011
  ExternalGeometry = -> [Pocket007]
  FullyConstrained = true
  MapMode = 5
  Placement = pos=(0,60,0) rot=(0,0.707107,0.707107;3.14159rad)
  Support = -> [Pocket007]
  sketch-geometry (2):
    g0: Circle CenterX=-50.6 CenterY=5.5 CenterZ=0 NormalX=0 NormalY=0 NormalZ=1 AngleXU=0 Radius=3
    g1: Circle CenterX=-35.6 CenterY=5.5 CenterZ=0 NormalX=0 NormalY=0 NormalZ=1 AngleXU=0 Radius=3
  constraints (4):
    c: Coincident(g0,g-3)
    c: Coincident(g1,g-4)
    c: Radius(g0) = 3
    c: Equal(g0,g1)
FEATURE [PartDesign::Pocket] Pocket008
  BaseFeature = -> Pocket007
  Length = 11
  Length2 = 100
  Profile = -> Sketch011
  Type = 0
FEATURE [Sketcher::SketchObject] Sketch012
  ExternalGeometry = -> [Pocket008]
  FullyConstrained = true
  MapMode = 5
  Placement = pos=(0,60,0) rot=(0,0.707107,0.707107;3.14159rad)
  Support = -> [Pocket008]
  sketch-geometry (6):
    g0: LineSegment StartX=-64.7018 StartY=11 StartZ=0 EndX=-20.3 EndY=11 EndZ=0
    g1: LineSegment StartX=-20.3 StartY=11 StartZ=0 EndX=-20.3 EndY=7.1 EndZ=0
    g2: LineSegment StartX=-22.3 StartY=5.1 StartZ=0 EndX=-62.7018 EndY=5.1 EndZ=0
    g3: LineSegment StartX=-64.7018 StartY=7.1 StartZ=0 EndX=-64.7018 EndY=11 EndZ=0
    g4: ArcOfCircle CenterX=-62.7018 CenterY=7.1 CenterZ=0 NormalX=0 NormalY=0 NormalZ=1 AngleXU=0 Radius=2 StartAngle=3.14159 EndAngle=4.71239
    g5: ArcOfCircle CenterX=-22.3 CenterY=7.1 CenterZ=0 NormalX=0 NormalY=0 NormalZ=1 AngleXU=0 Radius=2 StartAngle=4.71239 EndAngle=6.28319
  constraints (14):
    c: Coincident(g0,g1)
    c: Coincident(g3,g0)
    c: Horizontal(g2)
    c: Vertical(g1)
    c: Vertical(g3)
    c: Coincident(g0,g-3)
    c: Coincident(g0,g-4)
    c: Tangent(g3,g4) = 1.5708
    c: Tangent(g2,g4) = 1.5708
    c: Tangent(g2,g5) = 1.5708
    c: Tangent(g1,g5) = 1.5708
    c: Equal(g4,g5)
    c: DistanceY(g2,g0) = 5.9
    c: Radius(g4) = 2
FEATURE [PartDesign::Pocket] Pocket009
  BaseFeature = -> Pocket008
  Length = 8
  Length2 = 100
  Profile = -> Sketch012
  Type = 0
FEATURE [Sketcher::SketchObject] Sketch013
  ExternalGeometry = -> [Pocket009]
  FullyConstrained = true
  MapMode = 5
  Placement = pos=(0,0,0) rot=(0.57735,-0.57735,-0.57735;2.0944rad)
  Support = -> [Pocket009]
  sketch-geometry (4):
    g0: LineSegment StartX=-32.2 StartY=0 StartZ=0 EndX=-32.2 EndY=18 EndZ=0
    g1: LineSegment StartX=-32.2 StartY=18 StartZ=0 EndX=-27.2 EndY=18 EndZ=0
    g2: LineSegment StartX=-27.2 StartY=18 StartZ=0 EndX=-27.2 EndY=0 EndZ=0
    g3: LineSegment StartX=-27.2 StartY=0 StartZ=0 EndX=-32.2 EndY=0 EndZ=0
  constraints (12):
    c: PointOnObject(g0,g-1)
    c: Vertical(g0)
    c: Coincident(g0,g1)
    c: Horizontal(g1)
    c: Coincident(g1,g2)
    c: PointOnObject(g2,g-1)
    c: Vertical(g2)
    c: Coincident(g2,g3)
    c: Coincident(g3,g0)
    c: DistanceX(g1,g1) = 5
    c: DistanceX(g-3,g0) = 7.5
    c: Horizontal(g-3,g0)
FEATURE [PartDesign::Pad] Pad003
  BaseFeature = -> Pocket009
  Direction = (1,1,1)
  Length = 3
  Length2 = 100
  Profile = -> Sketch013
  Type = 0
FEATURE [PartDesign::Fillet] Fillet001
  Base = -> Pad003 [Edge287,Edge281,Edge286]
  BaseFeature = -> Pad003
  Radius = 2
  SupportTransform = false
FEATURE [Sketcher::SketchObject] Sketch014
  ExternalGeometry = -> [Fillet001]
  FullyConstrained = true
  MapMode = 5
  Placement = pos=(86,0,0) rot=(0.57735,0.57735,0.57735;2.0944rad)
  Support = -> [Fillet001]
  sketch-geometry (4):
    g0: LineSegment StartX=27.2 StartY=0 StartZ=0 EndX=32.2 EndY=0 EndZ=0
    g1: LineSegment StartX=32.2 StartY=0 StartZ=0 EndX=32.2 EndY=18 EndZ=0
    g2: LineSegment StartX=32.2 StartY=18 StartZ=0 EndX=27.2 EndY=18 EndZ=0
    g3: LineSegment StartX=27.2 StartY=18 StartZ=0 EndX=27.2 EndY=0 EndZ=0
  constraints (12):
    c: Coincident(g0,g1)
    c: Coincident(g1,g2)
    c: Coincident(g2,g3)
    c: Coincident(g3,g0)
    c: Horizontal(g0)
    c: Horizontal(g2)
    c: Vertical(g1)
    c: Vertical(g3)
    c: PointOnObject(g0,g-1)
    c: DistanceX(g2,g2) = 5
    c: DistanceX(g-3,g2) = 7.5
    c: Horizontal(g-3,g2)
FEATURE [PartDesign::Pad] Pad004
  BaseFeature = -> Fillet001
  Direction = (1,1,1)
  Length = 3
  Length2 = 100
  Profile = -> Sketch014
  Type = 0
FEATURE [PartDesign::Fillet] Fillet002
  Base = -> Pad004 [Edge279,Edge272,Edge278]
  BaseFeature = -> Pad004
  Radius = 2
  SupportTransform = false
FEATURE [PartDesign::Body] Body
  Group = -> [Sketch,Pad,Sketch001,Pad001,Sketch002,Pocket,Sketch003,Pocket001,Sketch004,Pocket002,Sketch005,Pocket003,Sketch006,Pad002,Sketch007,Pocket004,Sketch008,Pocket005,Sketch009,Pocket006,Sketch010,Pocket007,Sketch011,Pocket008,Sketch012,Pocket009,Sketch013,Pad003,Fillet001,Sketch014,Pad004,Fillet002]
  Origin = -> Origin
  Tip = -> Fillet002
FEATURE [Part::Fillet] Fillet
  Base = -> Pocket009
  Edges = 16 edges r=2: [Edge72,Edge86,Edge87,Edge172,Edge198,Edge199,Edge211,Edge216,Edge226,Edge235,Edge331,Edge347,Edge362,Edge375,Edge402,Edge411]
